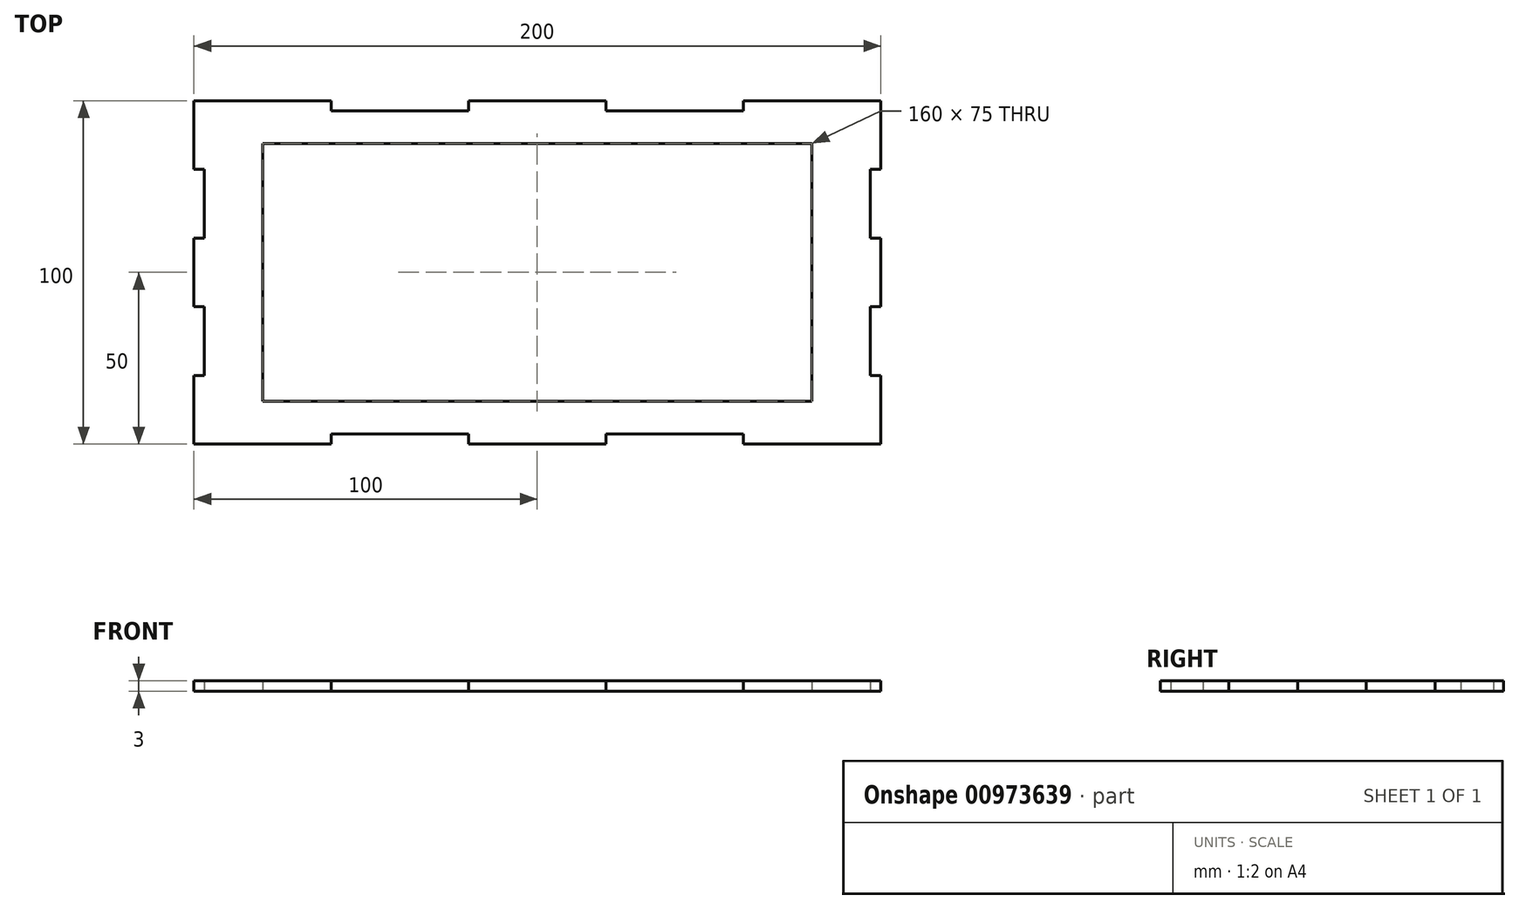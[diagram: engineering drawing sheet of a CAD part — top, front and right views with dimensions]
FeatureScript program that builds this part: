
annotation { "Feature Type Name" : "Feature", "Feature Type Description" : "" }
export const myFeature = defineFeature(function(context is Context, id is Id, definition is map)
    precondition{}
    {
        {
            var Q0;
            Q0=qCreatedBy(makeId("Top.planeOp"),FACE);
            var sketch = newSketch(context, id + "F0", { "sketchPlane" : qUnion([Q0])});
            skLineSegment(sketch, "E0", {"start": v(0, 0) * mm, "end": v(-200, 0) * mm});
            skLineSegment(sketch, "E1", {"start": v(-200, 0) * mm, "end": v(-200, -100) * mm});
            skLineSegment(sketch, "E2", {"start": v(-200, -100) * mm, "end": v(0, -100) * mm});
            skLineSegment(sketch, "E3", {"start": v(0, -100) * mm, "end": v(0, 0) * mm});
            skLineSegment(sketch, "E4", {"start": v(-200, -100) * mm, "end": v(-160, -100) * mm});
            skLineSegment(sketch, "E5", {"start": v(-120, -100) * mm, "end": v(-80, -100) * mm});
            skLineSegment(sketch, "E6", {"start": v(-200, 0) * mm, "end": v(-200, -20) * mm});
            skLineSegment(sketch, "E7", {"start": v(-200, -40) * mm, "end": v(-200, -60) * mm});
            skLineSegment(sketch, "E8", {"start": v(0, -40) * mm, "end": v(0, -60) * mm});
            skLineSegment(sketch, "E9", {"start": v(-100, -12.5) * mm, "end": v(-180, -12.5) * mm});
            skLineSegment(sketch, "E10", {"start": v(-180, -12.5) * mm, "end": v(-180, -87.5) * mm});
            skLineSegment(sketch, "E11", {"start": v(-180, -87.5) * mm, "end": v(-20, -87.5) * mm});
            skLineSegment(sketch, "E12", {"start": v(-20, -87.5) * mm, "end": v(-20, -12.5) * mm});
            skLineSegment(sketch, "E13", {"start": v(-20, -12.5) * mm, "end": v(-100, -12.5) * mm});
            skLineSegment(sketch, "E14", {"start": v(-160, -100) * mm, "end": v(-160, -97) * mm});
            skLineSegment(sketch, "E15", {"start": v(-160, -97) * mm, "end": v(-120, -97) * mm});
            skLineSegment(sketch, "E16", {"start": v(-80, -97) * mm, "end": v(-40, -97) * mm});
            skLineSegment(sketch, "E17", {"start": v(-200, -60) * mm, "end": v(-197, -60) * mm});
            skLineSegment(sketch, "E18", {"start": v(-197, -60) * mm, "end": v(-197, -80) * mm});
            skLineSegment(sketch, "E19", {"start": v(-197, -40) * mm, "end": v(-197, -20) * mm});
            skLineSegment(sketch, "E20", {"start": v(-160, 0) * mm, "end": v(-160, -3) * mm});
            skLineSegment(sketch, "E21", {"start": v(-160, -3) * mm, "end": v(-120, -3) * mm});
            skLineSegment(sketch, "E22", {"start": v(-80, -3) * mm, "end": v(-40, -3) * mm});
            skLineSegment(sketch, "E23", {"start": v(0, -20) * mm, "end": v(-3, -20) * mm});
            skLineSegment(sketch, "E24", {"start": v(-3, -20) * mm, "end": v(-3, -40) * mm});
            skLineSegment(sketch, "E25", {"start": v(-3, -60) * mm, "end": v(-3, -80) * mm});
            skLineSegment(sketch, "E26", {"start": v(-197, -20) * mm, "end": v(-200, -20) * mm});
            skLineSegment(sketch, "E27", {"start": v(-197, -40) * mm, "end": v(-200, -40) * mm});
            skLineSegment(sketch, "E28", {"start": v(-197, -80) * mm, "end": v(-200, -80) * mm});
            skLineSegment(sketch, "E29", {"start": v(-120, -97) * mm, "end": v(-120, -100) * mm});
            skLineSegment(sketch, "E30", {"start": v(-80, -97) * mm, "end": v(-80, -100) * mm});
            skLineSegment(sketch, "E31", {"start": v(-40, -97) * mm, "end": v(-40, -100) * mm});
            skLineSegment(sketch, "E32", {"start": v(-120, -3) * mm, "end": v(-120, 0) * mm});
            skLineSegment(sketch, "E33", {"start": v(-80, -3) * mm, "end": v(-80, 0) * mm});
            skLineSegment(sketch, "E34", {"start": v(-40, -3) * mm, "end": v(-40, 0) * mm});
            skLineSegment(sketch, "E35", {"start": v(-3, -40) * mm, "end": v(0, -40) * mm});
            skLineSegment(sketch, "E36", {"start": v(-3, -60) * mm, "end": v(0, -60) * mm});
            skLineSegment(sketch, "E37", {"start": v(-3, -80) * mm, "end": v(0, -80) * mm});
            skSolve(sketch);
        }
        {
            var Q0;
            Q0=makeQuery(id+"F0.imprint","IMPRINT",FACE,{"disambiguationData":[TD([[makeQuery(id+"F0.imprint","IMPRINT",EDGE,{"derivedFrom":sQuery(id+"F0.wireOp",EDGE,"E9")}),-1.0]])]});
            extrude(context, id + "F1", {"entities" : qUnion([Q0]), "depth" : 3 * mm, "offsetDistance" : 25 * mm});
        }
    });
